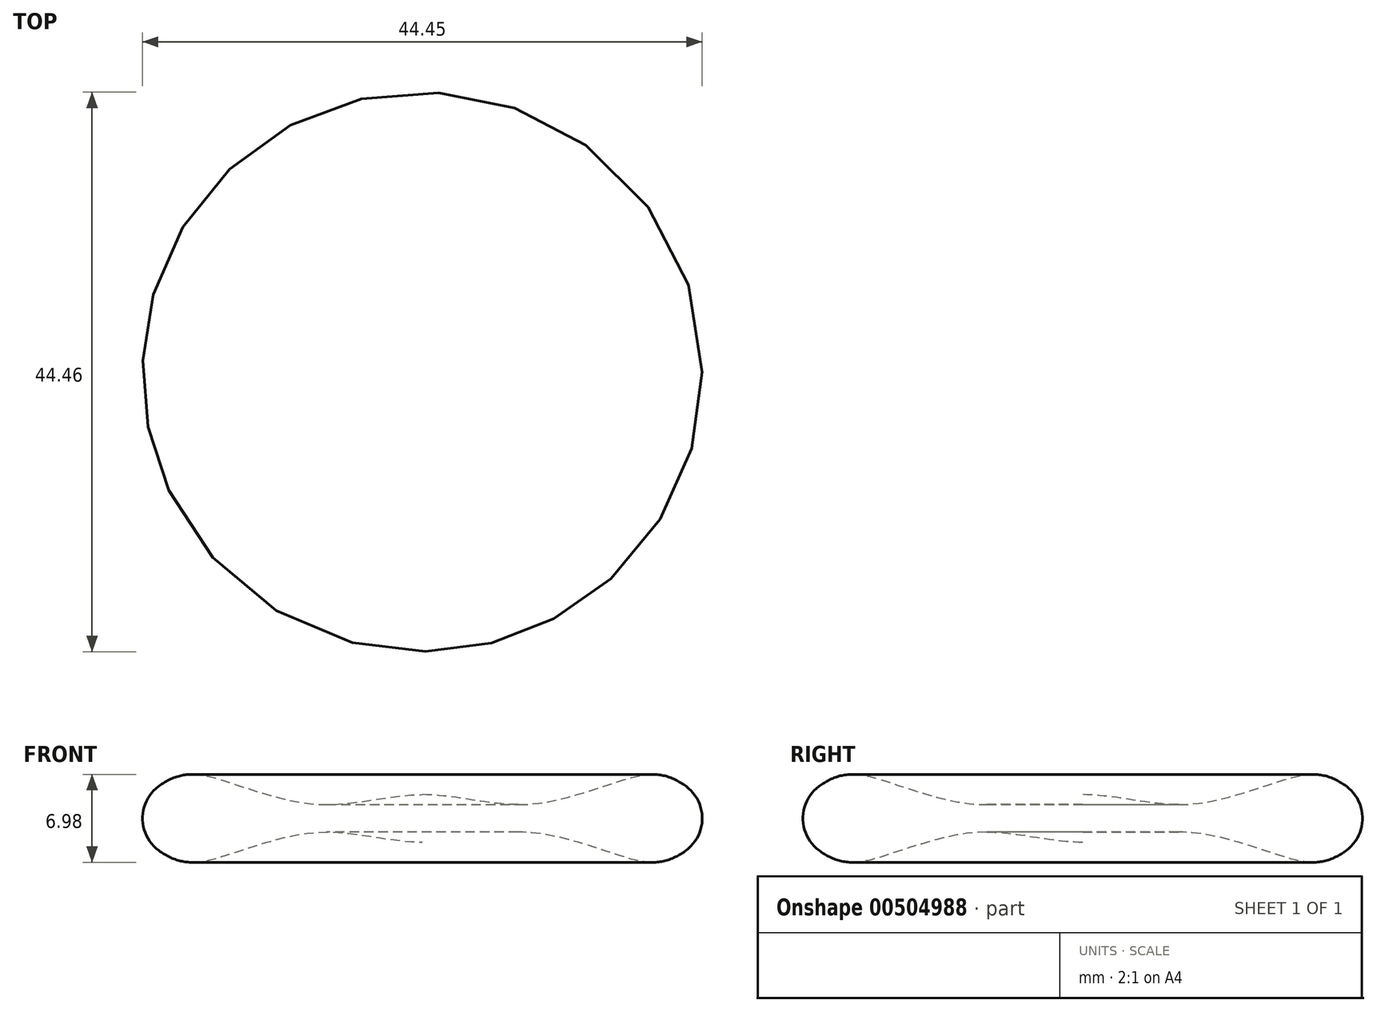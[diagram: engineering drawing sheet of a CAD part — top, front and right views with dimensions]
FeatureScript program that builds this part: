
annotation { "Feature Type Name" : "Feature", "Feature Type Description" : "" }
export const myFeature = defineFeature(function(context is Context, id is Id, definition is map)
    precondition{}
    {
        {
            var Q0;
            Q0=qCreatedBy(makeId("Front.planeOp"),FACE);
            var sketch = newSketch(context, id + "F0", { "sketchPlane" : qUnion([Q0])});
            skCircle(sketch, "E0", {"center": v(-19.05, 0) * mm, "radius": 3.18 * mm});
            skFitSpline(sketch, "E1", {"points": [v(-20.94, 2.55) * mm, v(-15.47, 2.9) * mm, v(-7.94, 1.1) * mm, v(0, 1.88) * mm], "startDerivative": vector(19.61, 14.59) * mm, "endDerivative": vector(23.96, 0.25) * mm});
            skFitSpline(sketch, "E2.MirrorCS", {"points": [v(-20.94, -2.55) * mm, v(-15.47, -2.9) * mm, v(-7.94, -1.1) * mm, v(0, -1.88) * mm], "startDerivative": vector(19.61, -14.59) * mm, "endDerivative": vector(23.96, -0.25) * mm});
            skLineSegment(sketch, "E3", {"start": v(0, 1.88) * mm, "end": v(0, -1.88) * mm});
            skSolve(sketch);
        }
        {
            var Q0;
            {var subQ0=sQuery(id+"F0.wireOp",EDGE,"E0");var subQ1=makeQuery(id+"F0.imprint","INTERSECT",VERTEX,{"derivedFrom":[subQ0,sQuery(id+"F0.wireOp",EDGE,"E1")]});Q0=makeQuery(id+"F0.imprint","IMPRINT",FACE,{"disambiguationData":[TD([[makeQuery(id+"F0.imprint","IMPRINT",EDGE,{"disambiguationData":[TD([[subQ1,-1.0]])],"derivedFrom":subQ0}),1.0]])]});}
            var Q1;
            {var subQ0=sQuery(id+"F0.wireOp",EDGE,"E1");Q1=makeQuery(id+"F0.imprint","IMPRINT",FACE,{"disambiguationData":[TD([[makeQuery(id+"F0.imprint","IMPRINT",EDGE,{"derivedFrom":subQ0}),-1.0]])]});}
            var Q2;
            Q2=sQuery(id+"F0.wireOp",EDGE,"E3");
            revolve(context, id + "F1", {"entities" : qUnion([Q0, Q1]), "axis" : qUnion([Q2]), "revolveType" : RevolveType.FULL});
        }
    });
